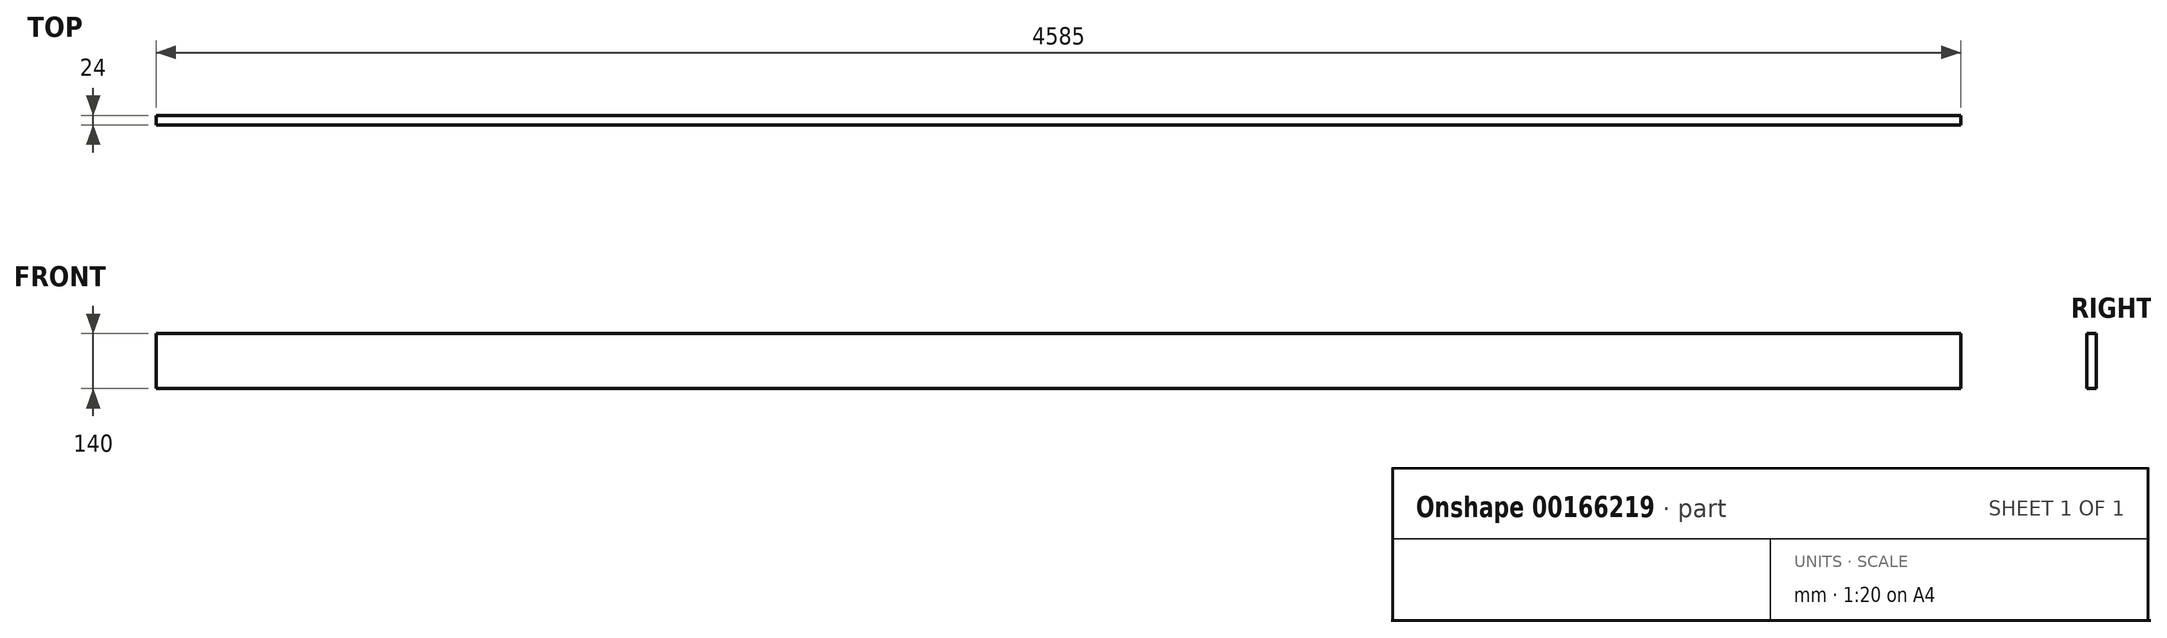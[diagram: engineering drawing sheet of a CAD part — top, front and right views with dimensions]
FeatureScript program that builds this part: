
annotation { "Feature Type Name" : "Feature", "Feature Type Description" : "" }
export const myFeature = defineFeature(function(context is Context, id is Id, definition is map)
    precondition{}
    {
        {
            var Q0;
            Q0=qCreatedBy(makeId("Front.planeOp"),FACE);
            var sketch = newSketch(context, id + "F0", { "sketchPlane" : qUnion([Q0])});
            skLineSegment(sketch, "E0.bottom", {"start": v(-2292.5, -70) * mm, "end": v(2292.5, -70) * mm});
            skLineSegment(sketch, "E0.top", {"start": v(-2292.5, 70) * mm, "end": v(2292.5, 70) * mm});
            skLineSegment(sketch, "E0.left", {"start": v(-2292.5, -70) * mm, "end": v(-2292.5, 70) * mm});
            skLineSegment(sketch, "E0.right", {"start": v(2292.5, -70) * mm, "end": v(2292.5, 70) * mm});
            skPoint(sketch, "E0.middle", {"position": v(0, 0) * mm});
            skSolve(sketch);
        }
        {
            var Q0;
            Q0=makeQuery(id+"F0.imprint","IMPRINT",FACE,{"disambiguationData":[TD([[makeQuery(id+"F0.imprint","IMPRINT",EDGE,{"derivedFrom":sQuery(id+"F0.wireOp",EDGE,"E0.bottom")}),1.0]])]});
            extrude(context, id + "F1", {"entities" : qUnion([Q0]), "depth" : 24 * mm, "symmetric" : true});
        }
    });
